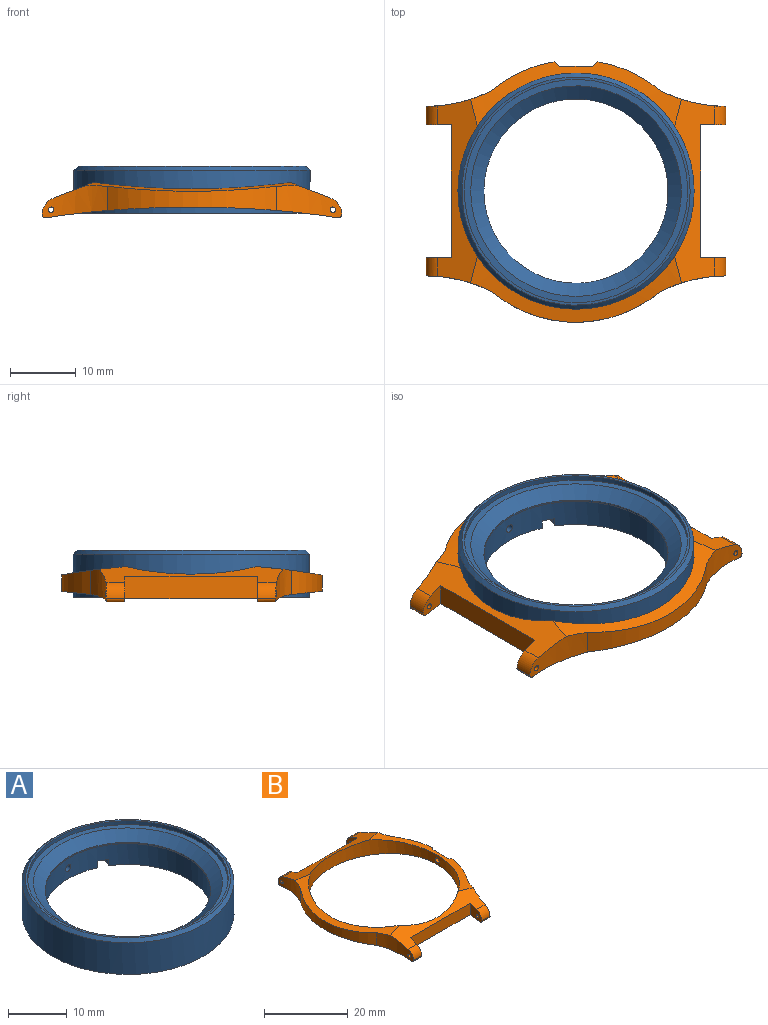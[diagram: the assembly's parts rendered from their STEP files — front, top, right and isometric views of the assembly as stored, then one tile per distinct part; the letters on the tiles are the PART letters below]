
ASSEMBLY  parts=2 mates=1
PART A: 29 faces, bbox 36x36x7.2 mm
  f0: cylinder r=14.35mm len=28.7mm, axis (0,0,-1), area 403.7mm2, adj f1,f2,f10,f11,f12,f14,f15,f16
  f1: plane 36x36mm, normal (0,0,-1), area 359.9mm2, adj f0,f3,f11,f12,f13,f15,f16,f17
  f2: plane 28.7x28.7mm, normal (0,0,-1), area 26.8mm2, adj f0,f8
  f3: cylinder r=18mm len=36mm, axis (0,0,-1), area 745.3mm2, adj f1,f9,f28
  f4: plane 34.8x34.8mm, normal (0,0,1), area 40.6mm2, adj f5,f9
  f5: cylinder r=17.02mm len=34.05mm, axis (0,0,-1), area 85.6mm2, adj f4,f6
  f6: plane 34.05x34.05mm, normal (0,0,1), area 101.3mm2, adj f5,f7
  f7: cone r=14.05mm half-angle=51.3deg, axis (0,0,1), area 242.2mm2, adj f6,f8
  f8: cylinder r=14.05mm len=28.1mm, axis (0,0,-1), area 22.1mm2, adj f2,f7
  f9: cone r=18mm half-angle=45deg, axis (0,0,-1), area 94.4mm2, adj f3,f4
  f10: plane 2.37x2.36mm, normal (0,0,-1), area 3.6mm2, adj f0,f11,f12,f13
  f11: plane 1.35x0.9mm, normal (0.88,-0.47,0), area 1.4mm2, adj f0,f1,f10,f13
  f12: plane 1.35x0.9mm, normal (-0.88,0.47,0), area 1.4mm2, adj f0,f1,f10,f13
  f13: cylinder r=1mm len=1.88mm, axis (0,0,-1), area 4.2mm2, adj f1,f10,f11,f12
  f14: plane 2.37x2.36mm, normal (0,0,-1), area 3.6mm2, adj f0,f15,f16,f17
  f15: plane 1.35x0.9mm, normal (0.88,-0.47,0), area 1.4mm2, adj f0,f1,f14,f17
  f16: plane 1.35x0.9mm, normal (-0.88,0.47,0), area 1.4mm2, adj f0,f1,f14,f17
  f17: cylinder r=1mm len=1.88mm, axis (0,0,-1), area 4.2mm2, adj f1,f14,f15,f16
  f18: cylinder r=0.5mm len=3mm, axis (0,0,-1), area 9.4mm2, adj f1,f19
  f19: plane 1x1mm, normal (0,0,-1), area 0.8mm2, adj f18
  f20: cylinder r=0.5mm len=3mm, axis (0,0,-1), area 9.4mm2, adj f1,f21
  f21: plane 1x1mm, normal (0,0,-1), area 0.8mm2, adj f20
  f22: cylinder r=0.5mm len=3mm, axis (0,0,-1), area 9.4mm2, adj f1,f23
  f23: plane 1x1mm, normal (0,0,-1), area 0.8mm2, adj f22
  f24: cylinder r=0.5mm len=3mm, axis (0,0,-1), area 9.4mm2, adj f1,f25
  f25: plane 1x1mm, normal (0,0,-1), area 0.8mm2, adj f24
  f26: cylinder r=0.5mm len=3mm, axis (0,0,-1), area 9.4mm2, adj f1,f27
  f27: plane 1x1mm, normal (0,0,-1), area 0.8mm2, adj f26
  f28: cylinder r=0.62mm len=3.66mm, axis (0,-1,0), area 14.3mm2, adj f0,f3
PART B: 35 faces, bbox 39.7x45.8x5.4 mm
  f0: extruded ~32.16x9.82mm, area 71.5mm2, adj f2,f3,f6,f11,f12,f17,f18,f23
  f1: extruded ~44.57x39.72mm, area 316.9mm2, adj f2,f3,f4,f6,f7,f8,f9,f10
  f2: cylinder r=20mm len=9.53mm, axis (0,0,-1), area 32mm2, adj f0,f1,f6,f24
  f3: cylinder r=22.19mm len=9.99mm, axis (0,0,-1), area 34.7mm2, adj f0,f1,f12,f17,f20,f29,f34
  f4: cylinder r=22.19mm len=9.99mm, axis (0,0,-1), area 34.7mm2, adj f1,f5,f13,f17,f19,f30,f33
  f5: extruded ~32.16x10.1mm, area 76.8mm2, adj f4,f7,f11,f13,f17,f18
  f6: cylinder r=22.19mm len=9.99mm, axis (0,0,-1), area 34.7mm2, adj f0,f1,f2,f18,f22,f27,f31
  f7: cylinder r=22.19mm len=9.99mm, axis (0,0,-1), area 34.7mm2, adj f1,f5,f13,f18,f21,f28,f32
  f8: plane 3.86x3.85mm, normal (-1,0,0), area 9.9mm2, adj f1,f9,f18,f22,f27,f31
  f9: plane 20.25x3.36mm, normal (0,1,0), area 68mm2, adj f1,f8,f10,f18
  f10: plane 3.86x3.85mm, normal (1,0,0), area 9.9mm2, adj f1,f9,f18,f21,f28,f32
  f11: cylinder r=18mm len=36mm, axis (0,0,-1), area 405.5mm2, adj f0,f1,f5,f17,f18,f26
  f12: cylinder r=20mm len=9.53mm, axis (0,0,-1), area 32mm2, adj f0,f1,f3,f25
  f13: cylinder r=20mm len=25.76mm, axis (0,0,-1), area 80.4mm2, adj f1,f4,f5,f7
  f14: plane 20.25x3.36mm, normal (0,-1,0), area 68mm2, adj f1,f15,f16,f17
  f15: plane 3.86x3.85mm, normal (-1,0,0), area 9.9mm2, adj f1,f14,f17,f20,f29,f34
  f16: plane 3.86x3.85mm, normal (1,0,0), area 9.9mm2, adj f1,f14,f17,f19,f30,f33
  f17: plane 28.01x6.13mm, normal (0,-0.36,0.93), area 83.3mm2, adj f0,f3,f4,f5,f11,f14,f15,f16
  f18: plane 28.01x6.14mm, normal (0,0.36,0.93), area 83.3mm2, adj f0,f5,f6,f7,f8,f9,f10,f11
  f19: cylinder r=0.42mm len=2.85mm, axis (1,0,0), area 7.6mm2, adj f4,f16
  f20: cylinder r=0.42mm len=2.85mm, axis (1,0,0), area 7.6mm2, adj f3,f15
  f21: cylinder r=0.42mm len=2.85mm, axis (1,0,0), area 7.6mm2, adj f7,f10
  f22: cylinder r=0.42mm len=2.85mm, axis (1,0,0), area 7.6mm2, adj f6,f8
  f23: plane 5.01x2.61mm, normal (1,0,0), area 11.8mm2, adj f0,f1,f24,f25,f26
  f24: plane 2.63x0.84mm, normal (0.78,-0.62,0), area 2.8mm2, adj f0,f1,f2,f23
  f25: plane 2.63x0.84mm, normal (0.78,0.62,0), area 2.8mm2, adj f0,f1,f12,f23
  f26: cylinder r=0.62mm len=1.25mm, axis (1,0,0), area 4.1mm2, adj f11,f23
  f27: cylinder r=2.7mm len=2.87mm, axis (1,0,0), area 9.2mm2, adj f6,f8,f18,f31
  f28: cylinder r=2.7mm len=2.87mm, axis (1,0,0), area 9.2mm2, adj f7,f10,f18,f32
  f29: cylinder r=2.7mm len=2.87mm, axis (-1,0,0), area 9.2mm2, adj f3,f15,f17,f34
  f30: cylinder r=2.7mm len=2.87mm, axis (-1,0,0), area 9.2mm2, adj f4,f16,f17,f33
  f31: cylinder r=0.5mm len=2.81mm, axis (1,0,0), area 2.4mm2, adj f1,f6,f8,f27
  f32: cylinder r=0.5mm len=2.81mm, axis (1,0,0), area 2.4mm2, adj f1,f7,f10,f28
  f33: cylinder r=0.5mm len=2.81mm, axis (1,0,0), area 2.4mm2, adj f1,f4,f16,f30
  f34: cylinder r=0.5mm len=2.81mm, axis (1,0,0), area 2.4mm2, adj f1,f3,f15,f29
PLACE A rot(axis=(0,0,-1),0deg) t=(35.7,-22.79,-9.71)mm
PLACE B rot(axis=(0,0,1),90deg) t=(35.7,-22.79,-10.71)mm fixed
MATE cylindrical A.f0 <-> B.f11  axis (0,0,-1) through (35.7,-22.79,-6.61)mm
